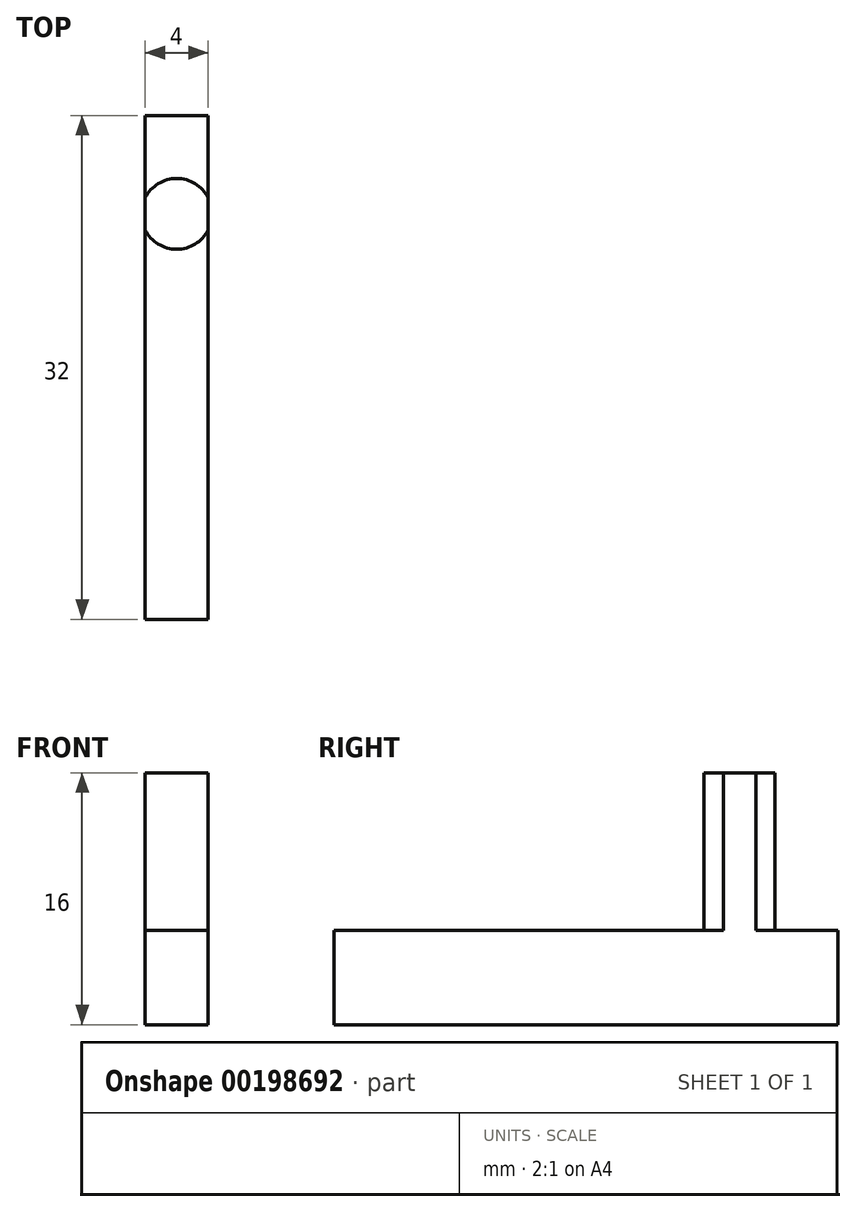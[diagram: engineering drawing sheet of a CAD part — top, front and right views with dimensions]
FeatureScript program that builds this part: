
annotation { "Feature Type Name" : "Feature", "Feature Type Description" : "" }
export const myFeature = defineFeature(function(context is Context, id is Id, definition is map)
    precondition{}
    {
        {
            var Q0;
            Q0=qCreatedBy(makeId("Top.planeOp"),FACE);
            var sketch = newSketch(context, id + "F0", { "sketchPlane" : qUnion([Q0])});
            skCircle(sketch, "E0", {"center": v(0, -6.25) * mm, "radius": 2.25 * mm});
            skLineSegment(sketch, "E1", {"start": v(0, -6.25) * mm, "end": v(0, -38.25) * mm, "construction": true});
            skLineSegment(sketch, "E2", {"start": v(-2.25, 0) * mm, "end": v(2.25, 0) * mm});
            skLineSegment(sketch, "E3", {"start": v(-2.25, 0) * mm, "end": v(-2.25, -32) * mm});
            skLineSegment(sketch, "E4", {"start": v(-2.25, -32) * mm, "end": v(2.25, -32) * mm});
            skLineSegment(sketch, "E5", {"start": v(2.25, -32) * mm, "end": v(2.25, 0) * mm});
            skSolve(sketch);
        }
        {
            var Q0;
            {var subQ0=sQuery(id+"F0.wireOp",EDGE,"E0");var subQ1=makeQuery(id+"F0.imprint","INTERSECT",VERTEX,{"derivedFrom":[subQ0,sQuery(id+"F0.wireOp",EDGE,"E3")]});Q0=makeQuery(id+"F0.imprint","IMPRINT",FACE,{"disambiguationData":[TD([[makeQuery(id+"F0.imprint","IMPRINT",EDGE,{"disambiguationData":[TD([[subQ1,1.0]])],"derivedFrom":subQ0}),1.0]])]});}
            extrude(context, id + "F1", {"entities" : qUnion([Q0]), "depth" : 10 * mm});
        }
        {
            var Q0;
            {var subQ0=sQuery(id+"F0.wireOp",EDGE,"E0");var subQ1=makeQuery(id+"F0.imprint","INTERSECT",VERTEX,{"derivedFrom":[subQ0,sQuery(id+"F0.wireOp",EDGE,"E3")]});Q0=makeQuery(id+"F0.imprint","IMPRINT",FACE,{"disambiguationData":[TD([[makeQuery(id+"F0.imprint","IMPRINT",EDGE,{"disambiguationData":[TD([[subQ1,1.0]])],"derivedFrom":subQ0}),1.0]])]});}
            var Q1;
            {var subQ5=sQuery(id+"F0.wireOp",EDGE,"E2");Q1=makeQuery(id+"F0.imprint","IMPRINT",FACE,{"disambiguationData":[TD([[makeQuery(id+"F0.imprint","IMPRINT",EDGE,{"derivedFrom":subQ5}),-1.0]])]});}
            var Q2;
            {var subQ5=sQuery(id+"F0.wireOp",EDGE,"E4");Q2=makeQuery(id+"F0.imprint","IMPRINT",FACE,{"disambiguationData":[TD([[makeQuery(id+"F0.imprint","IMPRINT",EDGE,{"derivedFrom":subQ5}),1.0]])]});}
            extrude(context, id + "F2", {"entities" : qUnion([Q0, Q1, Q2]), "operationType" : NewBodyOperationType.ADD, "oppositeDirection" : true, "depth" : 6 * mm});
        }
        {
            var Q0;
            Q0=makeQuery(id+"F2.opExtrude","CAP_FACE",FACE,{"disambiguationData":[OSD([sQuery(id+"F0.wireOp",EDGE,"E2"),sQuery(id+"F0.wireOp",EDGE,"E3"),sQuery(id+"F0.wireOp",EDGE,"E4"),sQuery(id+"F0.wireOp",EDGE,"E5")])],"isStart":false});
            var sketch = newSketch(context, id + "F3", { "sketchPlane" : qUnion([Q0])});
            skLineSegment(sketch, "E6.bottom", {"start": v(-2, 32) * mm, "end": v(2, 32) * mm});
            skLineSegment(sketch, "E6.top", {"start": v(-2, 0) * mm, "end": v(2, 0) * mm});
            skLineSegment(sketch, "E6.left", {"start": v(-2, 32) * mm, "end": v(-2, 0) * mm});
            skLineSegment(sketch, "E6.right", {"start": v(2, 32) * mm, "end": v(2, 0) * mm});
            skSolve(sketch);
        }
        {
            var Q0;
            Q0 = qSketchRegion(id + "F3", true);
            extrude(context, id + "F4", {"entities" : qUnion([Q0]), "operationType" : NewBodyOperationType.INTERSECT, "endBound" : BoundingType.THROUGH_ALL, "oppositeDirection" : true, "depth" : 25 * mm});
        }
    });
